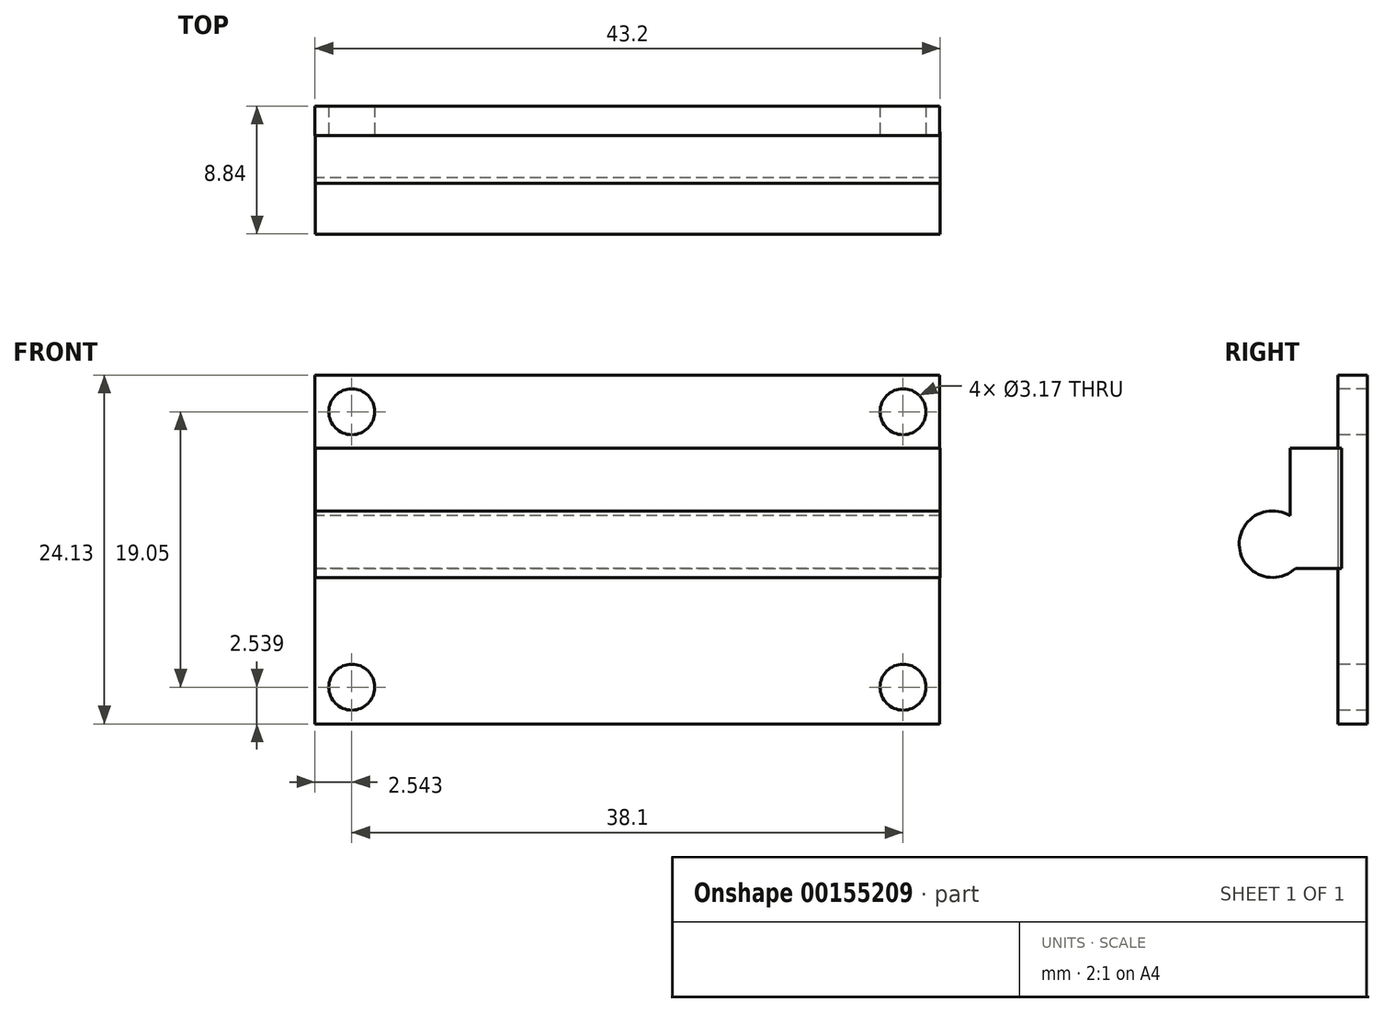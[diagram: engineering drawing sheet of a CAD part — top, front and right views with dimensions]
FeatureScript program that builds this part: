
annotation { "Feature Type Name" : "Feature", "Feature Type Description" : "" }
export const myFeature = defineFeature(function(context is Context, id is Id, definition is map)
    precondition{}
    {
        {
            var Q0;
            Q0=qCreatedBy(makeId("Front.planeOp"),FACE);
            var sketch = newSketch(context, id + "F0", { "sketchPlane" : qUnion([Q0])});
            skLineSegment(sketch, "E0.bottom", {"start": v(-20.09, 11.06) * mm, "end": v(23.1, 11.06) * mm});
            skLineSegment(sketch, "E0.top", {"start": v(-20.09, -13.07) * mm, "end": v(23.1, -13.07) * mm});
            skLineSegment(sketch, "E0.left", {"start": v(-20.09, 11.06) * mm, "end": v(-20.09, -13.07) * mm});
            skLineSegment(sketch, "E0.right", {"start": v(23.1, 11.06) * mm, "end": v(23.1, -13.07) * mm});
            skCircle(sketch, "E1", {"center": v(-17.55, 8.52) * mm, "radius": 1.59 * mm});
            skCircle(sketch, "E2", {"center": v(20.55, 8.52) * mm, "radius": 1.59 * mm});
            skCircle(sketch, "E3", {"center": v(-17.55, -10.53) * mm, "radius": 1.59 * mm});
            skCircle(sketch, "E4", {"center": v(20.55, -10.53) * mm, "radius": 1.59 * mm});
            skLineSegment(sketch, "E5.bottom", {"start": v(-20.09, 5.98) * mm, "end": v(23.1, 5.98) * mm});
            skLineSegment(sketch, "E5.top", {"start": v(-20.09, -8) * mm, "end": v(23.1, -8) * mm});
            skLineSegment(sketch, "E5.left", {"start": v(-20.09, 5.98) * mm, "end": v(-20.09, -8) * mm});
            skLineSegment(sketch, "E5.right", {"start": v(23.1, 5.98) * mm, "end": v(23.1, -8) * mm});
            skSolve(sketch);
        }
        {
            var Q0;
            Q0=qCreatedBy(makeId("Right.planeOp"),FACE);
            var sketch = newSketch(context, id + "F1", { "sketchPlane" : qUnion([Q0])});
            skLineSegment(sketch, "E6.bottom", {"start": v(0, 6.01) * mm, "end": v(-9.52, 6.01) * mm});
            skLineSegment(sketch, "E6.top", {"start": v(0, -7.96) * mm, "end": v(-9.52, -7.96) * mm});
            skLineSegment(sketch, "E6.left", {"start": v(0, 6.01) * mm, "end": v(0, -7.96) * mm});
            skLineSegment(sketch, "E6.right", {"start": v(-9.53, 6.01) * mm, "end": v(-9.52, -7.96) * mm});
            skLineSegment(sketch, "E7.bottom", {"start": v(0.33, 6.01) * mm, "end": v(-3.56, 6.01) * mm});
            skArc(sketch, "E8", {"start": v(-3.56, 1.32) * mm, "mid": v(-7.05, -0.88) * mm, "end": v(-3.18, -2.31) * mm});
            skLineSegment(sketch, "E9", {"start": v(-3.56, 1.32) * mm, "end": v(-3.56, 6.01) * mm});
            skLineSegment(sketch, "E10", {"start": v(-3.18, -2.31) * mm, "end": v(0, -2.31) * mm});
            skSolve(sketch);
        }
        {
            var Q0;
            Q0=makeQuery(id+"F1.imprint","IMPRINT",FACE,{"disambiguationData":[TD([[makeQuery(id+"F1.imprint","IMPRINT",EDGE,{"derivedFrom":sQuery(id+"F1.wireOp",EDGE,"E6.bottom")}),1.0]])]});
            extrude(context, id + "F2", {"entities" : qUnion([Q0]), "depth" : 23.1 * mm, "hasSecondDirection" : true, "secondDirectionOppositeDirection" : true, "secondDirectionDepth" : 20.07 * mm});
        }
        {
            var Q0;
            Q0 = qSketchRegion(id + "F0", true);
            extrude(context, id + "F3", {"entities" : qUnion([Q0]), "operationType" : NewBodyOperationType.ADD, "oppositeDirection" : true, "depth" : 1.78 * mm, "hasSecondDirection" : true, "secondDirectionOppositeDirection" : false, "secondDirectionDepth" : 0.25 * mm});
        }
    });
